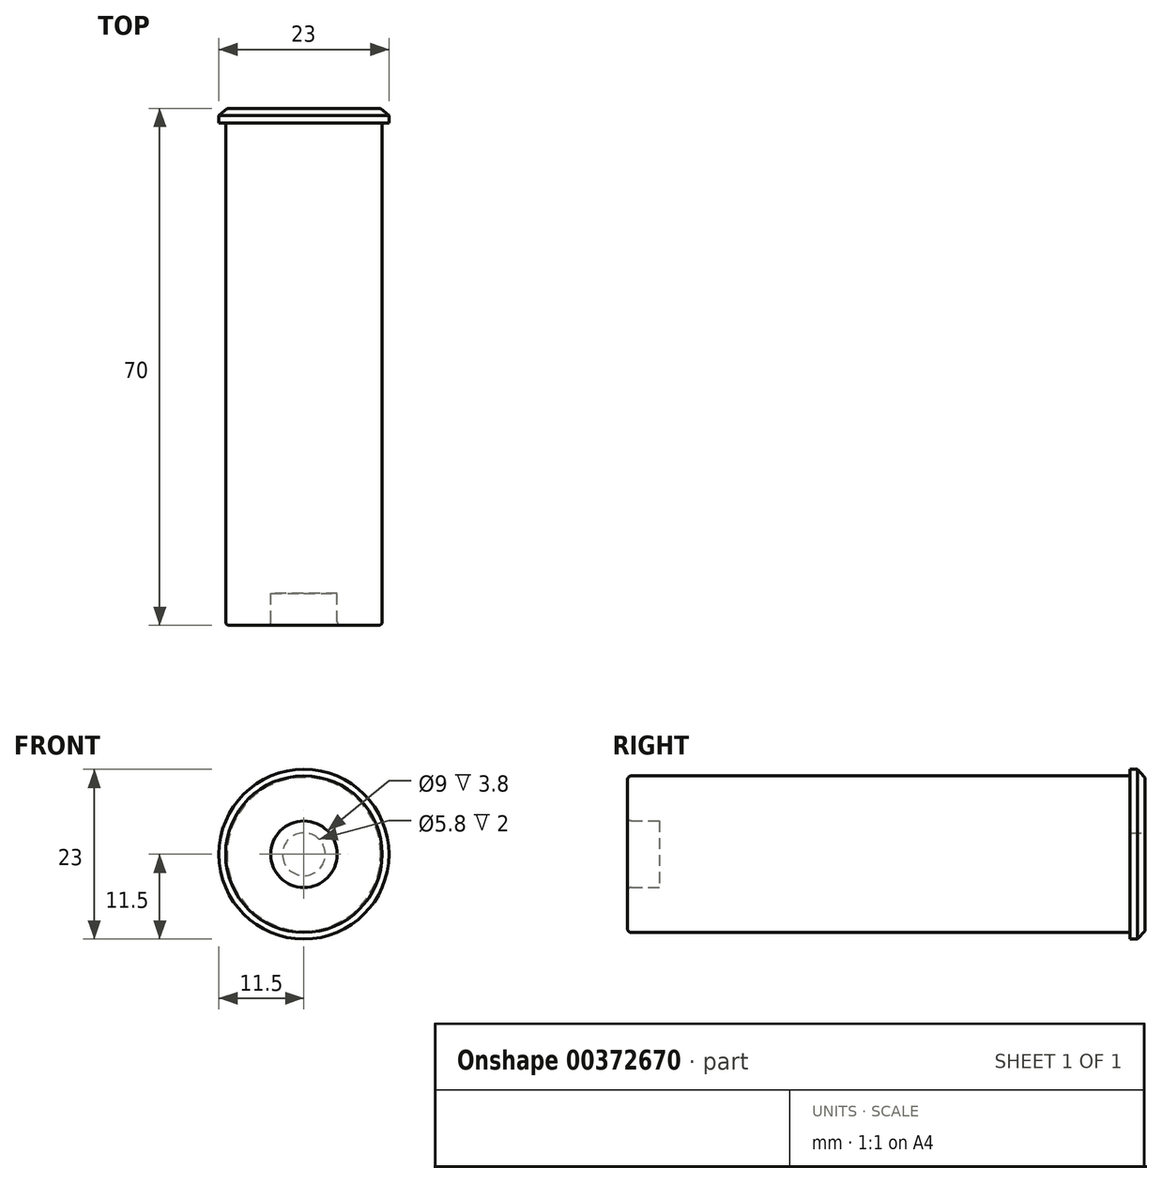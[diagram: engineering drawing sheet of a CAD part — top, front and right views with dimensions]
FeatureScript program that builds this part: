
annotation { "Feature Type Name" : "Feature", "Feature Type Description" : "" }
export const myFeature = defineFeature(function(context is Context, id is Id, definition is map)
    precondition{}
    {
        {
            var Q0;
            Q0=qCreatedBy(makeId("Top.planeOp"),FACE);
            var sketch = newSketch(context, id + "F0", { "sketchPlane" : qUnion([Q0])});
            skLineSegment(sketch, "E0", {"start": v(0, -2) * mm, "end": v(0, -65.7) * mm});
            skLineSegment(sketch, "E1", {"start": v(4.5, -70) * mm, "end": v(10.6, -70) * mm});
            skLineSegment(sketch, "E2", {"start": v(10.6, -70) * mm, "end": v(10.6, -2) * mm});
            skLineSegment(sketch, "E3", {"start": v(10.6, -2) * mm, "end": v(11.5, -2) * mm});
            skLineSegment(sketch, "E4", {"start": v(11.5, -2) * mm, "end": v(11.5, -1) * mm});
            skLineSegment(sketch, "E5", {"start": v(11.5, -1) * mm, "end": v(10.4, 0) * mm});
            skLineSegment(sketch, "E6", {"start": v(10.4, 0) * mm, "end": v(2.9, 0) * mm});
            skLineSegment(sketch, "E7", {"start": v(4.5, -70) * mm, "end": v(4.5, -65.7) * mm});
            skLineSegment(sketch, "E8", {"start": v(4.5, -65.7) * mm, "end": v(0, -65.7) * mm});
            skLineSegment(sketch, "E9", {"start": v(2.9, 0) * mm, "end": v(2.9, -2) * mm});
            skLineSegment(sketch, "E10", {"start": v(2.9, -2) * mm, "end": v(0, -2) * mm});
            skSolve(sketch);
        }
        {
            var Q0;
            Q0=makeQuery(id+"F0.imprint","IMPRINT",FACE,{"disambiguationData":[TD([[makeQuery(id+"F0.imprint","IMPRINT",EDGE,{"derivedFrom":sQuery(id+"F0.wireOp",EDGE,"E0")}),1.0]])]});
            var Q1;
            Q1=sQuery(id+"F0.wireOp",EDGE,"E0");
            revolve(context, id + "F1", {"surfaceOperationType" : NewSurfaceOperationType.NEW, "entities" : qUnion([Q0]), "axis" : qUnion([Q1]), "revolveType" : RevolveType.FULL});
        }
        {
            var Q0;
            Q0=makeQuery(id+"F1.opRevolve","SWEPT_EDGE",EDGE,{"disambiguationData":[OSD([sQuery(id+"F0.wireOp",EDGE,"E1"),sQuery(id+"F0.wireOp",EDGE,"E2")])]});
            var Q1;
            Q1=makeQuery(id+"F1.opRevolve","SWEPT_EDGE",EDGE,{"disambiguationData":[OSD([sQuery(id+"F0.wireOp",EDGE,"E1"),sQuery(id+"F0.wireOp",EDGE,"E7")])]});
            fillet(context, id + "F2", {"entities" : qUnion([Q0, Q1]), "radius" : 0.5 * mm, "tangentPropagation" : true, "allowEdgeOverflow" : false});
        }
    });
